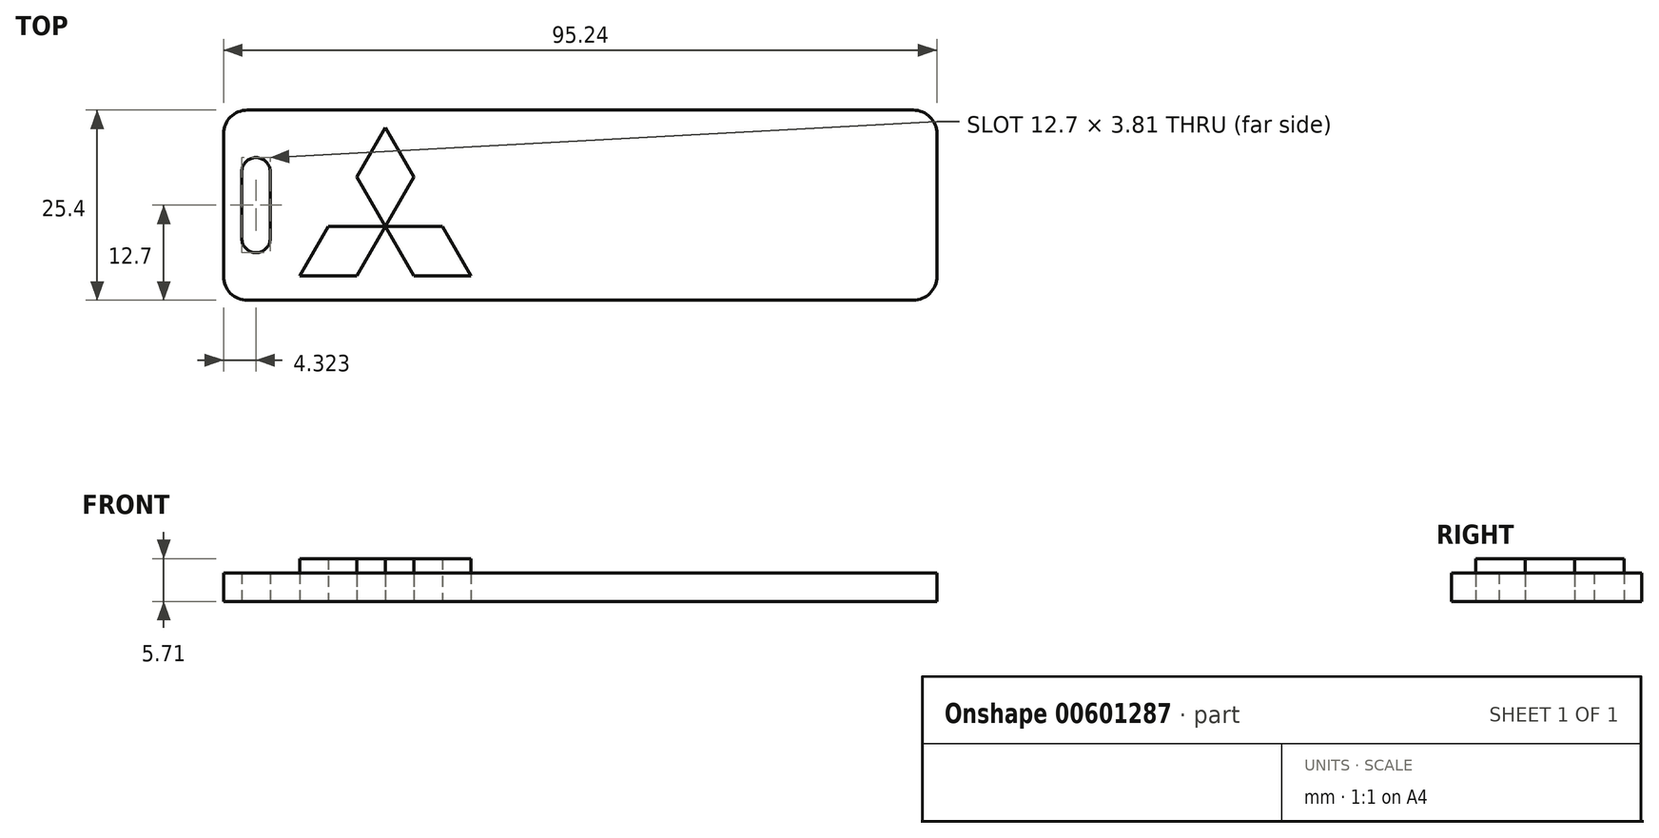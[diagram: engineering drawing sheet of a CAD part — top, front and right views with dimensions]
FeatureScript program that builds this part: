
annotation { "Feature Type Name" : "Feature", "Feature Type Description" : "" }
export const myFeature = defineFeature(function(context is Context, id is Id, definition is map)
    precondition{}
    {
        {
            var Q0;
            Q0=qCreatedBy(makeId("Top.planeOp"),FACE);
            var sketch = newSketch(context, id + "F0", { "sketchPlane" : qUnion([Q0])});
            skLineSegment(sketch, "E0.bottom", {"start": v(44.45, -12.7) * mm, "end": v(-44.45, -12.7) * mm});
            skLineSegment(sketch, "E0.top", {"start": v(44.45, 12.7) * mm, "end": v(-44.45, 12.7) * mm});
            skLineSegment(sketch, "E0.left", {"start": v(47.63, -9.53) * mm, "end": v(47.63, 9.52) * mm});
            skLineSegment(sketch, "E0.right", {"start": v(-47.63, -9.52) * mm, "end": v(-47.63, 9.53) * mm});
            skPoint(sketch, "E0.middle", {"position": v(0, 0) * mm});
            skPoint(sketch, "E1.visualSharp", {"position": v(-47.63, 12.7) * mm});
            skArc(sketch, "E1.filletArc", {"start": v(-44.45, 12.7) * mm, "mid": v(-46.7, 11.77) * mm, "end": v(-47.63, 9.53) * mm});
            skPoint(sketch, "E2.visualSharp", {"position": v(47.63, 12.7) * mm});
            skArc(sketch, "E2.filletArc", {"start": v(47.63, 9.52) * mm, "mid": v(46.7, 11.77) * mm, "end": v(44.45, 12.7) * mm});
            skPoint(sketch, "E3.visualSharp", {"position": v(47.63, -12.7) * mm});
            skArc(sketch, "E3.filletArc", {"start": v(44.45, -12.7) * mm, "mid": v(46.7, -11.77) * mm, "end": v(47.63, -9.53) * mm});
            skPoint(sketch, "E4.visualSharp", {"position": v(-47.63, -12.7) * mm});
            skArc(sketch, "E4.filletArc", {"start": v(-47.63, -9.52) * mm, "mid": v(-46.7, -11.77) * mm, "end": v(-44.45, -12.7) * mm});
            skLineSegment(sketch, "E5.bottom", {"start": v(-43.3, -6.35) * mm, "end": v(-43.3, -6.35) * mm});
            skLineSegment(sketch, "E5.top", {"start": v(-43.3, 6.35) * mm, "end": v(-43.3, 6.35) * mm});
            skLineSegment(sketch, "E5.left", {"start": v(-41.4, -4.45) * mm, "end": v(-41.4, 4.44) * mm});
            skLineSegment(sketch, "E5.right", {"start": v(-45.2, -4.45) * mm, "end": v(-45.2, 4.44) * mm});
            skPoint(sketch, "E5.middle", {"position": v(-43.3, 0) * mm});
            skPoint(sketch, "E6.visualSharp", {"position": v(-41.4, 6.35) * mm});
            skArc(sketch, "E6.filletArc", {"start": v(-41.4, 4.44) * mm, "mid": v(-41.95, 5.8) * mm, "end": v(-43.3, 6.35) * mm});
            skPoint(sketch, "E7.visualSharp", {"position": v(-45.2, 6.35) * mm});
            skArc(sketch, "E7.filletArc", {"start": v(-43.3, 6.35) * mm, "mid": v(-44.64, 5.8) * mm, "end": v(-45.2, 4.44) * mm});
            skPoint(sketch, "E8.visualSharp", {"position": v(-45.2, -6.35) * mm});
            skArc(sketch, "E8.filletArc", {"start": v(-45.2, -4.45) * mm, "mid": v(-44.64, -5.8) * mm, "end": v(-43.3, -6.35) * mm});
            skPoint(sketch, "E9.visualSharp", {"position": v(-41.4, -6.35) * mm});
            skArc(sketch, "E9.filletArc", {"start": v(-43.3, -6.35) * mm, "mid": v(-41.95, -5.8) * mm, "end": v(-41.4, -4.45) * mm});
            skLineSegment(sketch, "E10.bottom", {"start": v(43.81, -10.8) * mm, "end": v(-43.82, -10.8) * mm});
            skLineSegment(sketch, "E10.top", {"start": v(43.82, 10.8) * mm, "end": v(-43.82, 10.8) * mm});
            skLineSegment(sketch, "E10.left", {"start": v(45.72, -8.9) * mm, "end": v(45.72, 8.9) * mm});
            skLineSegment(sketch, "E10.right", {"start": v(-45.72, -8.9) * mm, "end": v(-45.72, 8.9) * mm});
            skPoint(sketch, "E11.visualSharp", {"position": v(45.72, -10.8) * mm});
            skArc(sketch, "E11.filletArc", {"start": v(43.81, -10.8) * mm, "mid": v(45.16, -10.24) * mm, "end": v(45.72, -8.9) * mm});
            skPoint(sketch, "E12.visualSharp", {"position": v(45.72, 10.8) * mm});
            skArc(sketch, "E12.filletArc", {"start": v(45.72, 8.9) * mm, "mid": v(45.16, 10.24) * mm, "end": v(43.82, 10.8) * mm});
            skPoint(sketch, "E13.visualSharp", {"position": v(-45.72, 10.8) * mm});
            skArc(sketch, "E13.filletArc", {"start": v(-43.82, 10.8) * mm, "mid": v(-45.16, 10.24) * mm, "end": v(-45.72, 8.9) * mm});
            skPoint(sketch, "E14.visualSharp", {"position": v(-45.72, -10.8) * mm});
            skArc(sketch, "E14.filletArc", {"start": v(-45.72, -8.9) * mm, "mid": v(-45.16, -10.24) * mm, "end": v(-43.82, -10.8) * mm});
            skSolve(sketch);
        }
        {
            var Q0;
            Q0=qCreatedBy(makeId("Top.planeOp"),FACE);
            var sketch = newSketch(context, id + "F1", { "sketchPlane" : qUnion([Q0])});
            skLineSegment(sketch, "E15", {"start": v(-26.01, -2.86) * mm, "end": v(-29.82, 3.74) * mm});
            skLineSegment(sketch, "E16", {"start": v(-29.82, 3.74) * mm, "end": v(-26.01, 10.34) * mm});
            skLineSegment(sketch, "E17", {"start": v(-26.01, 10.34) * mm, "end": v(-22.2, 3.74) * mm});
            skLineSegment(sketch, "E18", {"start": v(-22.2, 3.74) * mm, "end": v(-26.01, -2.86) * mm});
            skLineSegment(sketch, "E19.1.0", {"start": v(-29.82, -9.46) * mm, "end": v(-37.44, -9.46) * mm});
            skLineSegment(sketch, "E19.1.1", {"start": v(-37.44, -9.46) * mm, "end": v(-33.63, -2.86) * mm});
            skLineSegment(sketch, "E19.1.2", {"start": v(-26.01, -2.86) * mm, "end": v(-29.82, -9.46) * mm});
            skLineSegment(sketch, "E19.1.3", {"start": v(-33.63, -2.86) * mm, "end": v(-26.01, -2.86) * mm});
            skLineSegment(sketch, "E19.2.0", {"start": v(-18.4, -2.86) * mm, "end": v(-14.58, -9.46) * mm});
            skLineSegment(sketch, "E19.2.1", {"start": v(-14.58, -9.46) * mm, "end": v(-22.2, -9.46) * mm});
            skLineSegment(sketch, "E19.2.2", {"start": v(-26.01, -2.86) * mm, "end": v(-18.4, -2.86) * mm});
            skLineSegment(sketch, "E19.2.3", {"start": v(-22.2, -9.46) * mm, "end": v(-26.01, -2.86) * mm});
            skPoint(sketch, "E19.center", {"position": v(-26.01, -2.86) * mm});
            skSolve(sketch);
        }
        {
            var Q0;
            Q0=makeQuery(id+"F0.imprint","IMPRINT",FACE,{"disambiguationData":[TD([[makeQuery(id+"F0.imprint","IMPRINT",EDGE,{"derivedFrom":sQuery(id+"F0.wireOp",EDGE,"E0.bottom")}),-1.0]])]});
            var Q1;
            Q1=makeQuery(id+"F0.imprint","IMPRINT",FACE,{"disambiguationData":[TD([[makeQuery(id+"F0.imprint","IMPRINT",EDGE,{"derivedFrom":sQuery(id+"F0.wireOp",EDGE,"E5.left")}),-1.0]])]});
            extrude(context, id + "F2", {"entities" : qUnion([Q0, Q1]), "depth" : 3.8 * mm, "offsetDistance" : 25.4 * mm});
        }
        {
            var Q0;
            Q0 = qSketchRegion(id + "F1", true);
            extrude(context, id + "F3", {"entities" : qUnion([Q0]), "depth" : 5.7 * mm, "offsetDistance" : 25.4 * mm});
        }
    });
